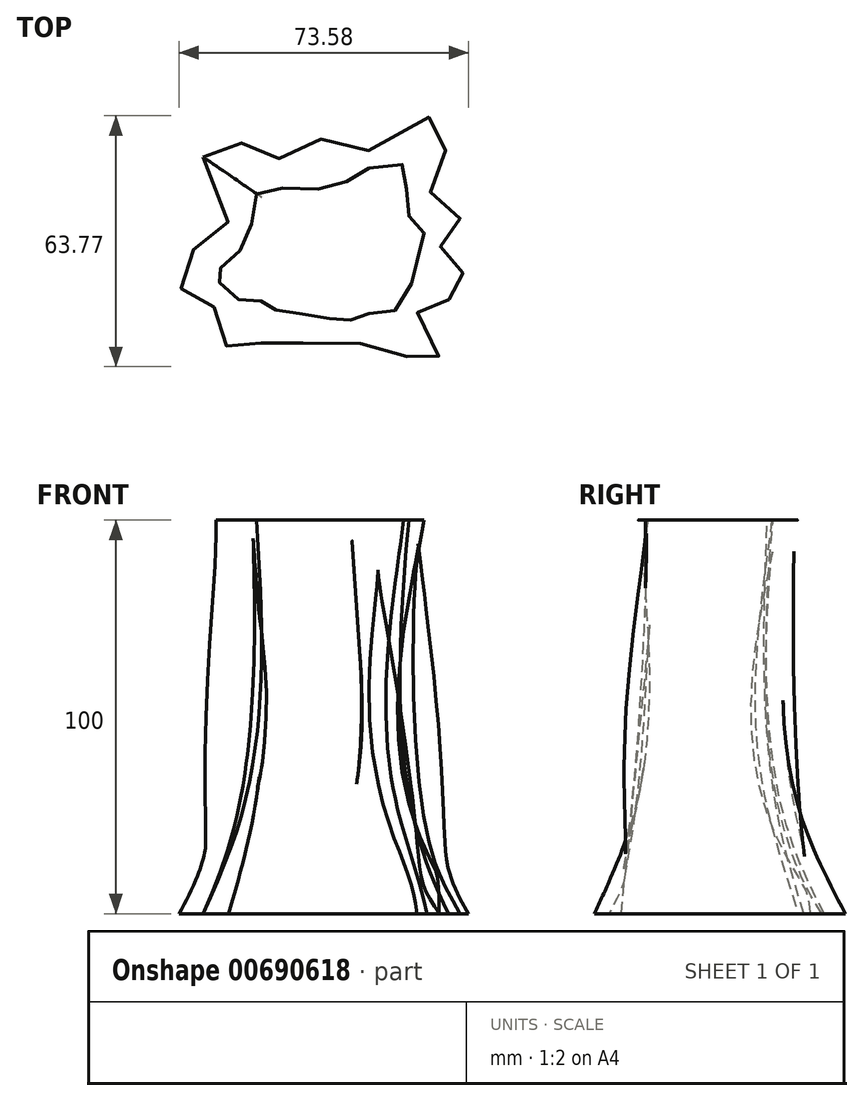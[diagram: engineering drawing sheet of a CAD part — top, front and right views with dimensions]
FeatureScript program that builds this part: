
annotation { "Feature Type Name" : "Feature", "Feature Type Description" : "" }
export const myFeature = defineFeature(function(context is Context, id is Id, definition is map)
    precondition{}
    {
        {
            var Q0;
            Q0=qCreatedBy(makeId("Top.planeOp"),FACE);
            var sketch = newSketch(context, id + "F0", { "sketchPlane" : qUnion([Q0])});
            skFitSpline(sketch, "E0", {"points": [v(-31.72, 26.3) * mm, v(-25.3, 7.86) * mm, v(-34.11, 2.83) * mm, v(-37.88, -4.72) * mm, v(-34.74, -9.75) * mm, v(-28.45, -12.26) * mm, v(-26.77, -20.11) * mm, v(-21.81, -23.2) * mm, v(-15.88, -20.43) * mm, v(-8.2, -20.73) * mm, v(6.04, -21.09) * mm, v(17.8, -22.59) * mm, v(23.98, -26.92) * mm, v(28.31, -23.2) * mm, v(22.74, -13.3) * mm, v(24.24, -10.32) * mm, v(33.88, -8.97) * mm, v(35.12, -4.02) * mm, v(28.77, 0) * mm, v(29.55, 5.26) * mm, v(33.26, 8.97) * mm, v(31.4, 15.16) * mm, v(25.22, 18.26) * mm, v(30.17, 28.78) * mm, v(27.7, 36.82) * mm, v(10.98, 28.16) * mm, v(0, 30.63) * mm, v(-8.2, 28.78) * mm, v(-16.25, 25.06) * mm, v(-24.3, 31.25) * mm, v(-31.72, 26.3) * mm]});
            skSolve(sketch);
        }
        {
            var Q0;
            Q0=qCreatedBy(makeId("Top.planeOp"),FACE);
            cPlane(context, id + "F1", {"entities" : qUnion([Q0]), "cplaneType" : CPlaneType.OFFSET, "offset" : 100 * mm, "width" : 150 * mm, "height" : 150 * mm});
        }
        {
            var Q0;
            Q0=qCreatedBy(id+"F1.planeOp",FACE);
            var sketch = newSketch(context, id + "F2", { "sketchPlane" : qUnion([Q0])});
            skFitSpline(sketch, "E1", {"points": [v(-17.91, 17.21) * mm, v(-19.82, 6.71) * mm, v(-25.23, 0) * mm, v(-28.41, -3.78) * mm, v(-26.5, -6.65) * mm, v(-20.27, -10.83) * mm, v(-15.32, -10.21) * mm, v(-12.19, -13.33) * mm, v(-3.57, -13.3) * mm, v(4.48, -15.78) * mm, v(7.86, -13.33) * mm, v(15.02, -13.8) * mm, v(21.22, -5.7) * mm, v(22.65, 0) * mm, v(24.08, 8.62) * mm, v(19.31, 12.92) * mm, v(20.26, 23.42) * mm, v(10.24, 23.42) * mm, v(3.56, 19.6) * mm, v(-8.37, 18.17) * mm, v(-17.91, 17.21) * mm]});
            skSolve(sketch);
        }
        {
            var Q0;
            Q0=qCreatedBy(makeId("Top.planeOp"),FACE);
            cPlane(context, id + "F3", {"entities" : qUnion([Q0]), "cplaneType" : CPlaneType.OFFSET, "offset" : 20 * mm, "width" : 150 * mm, "height" : 150 * mm});
        }
        {
            var Q0;
            Q0=qCreatedBy(id+"F3.planeOp",FACE);
            var sketch = newSketch(context, id + "F4", { "sketchPlane" : qUnion([Q0])});
            skFitSpline(sketch, "E2", {"points": [v(-24.3, 17.64) * mm, v(-20.04, 9.69) * mm, v(-20.89, 6.57) * mm, v(-22.45, 5.1) * mm, v(-26.85, 2.31) * mm, v(-30.11, -1.42) * mm, v(-30.68, -2.56) * mm, v(-30.96, -4.55) * mm, v(-28.41, -6.82) * mm, v(-25.57, -9.37) * mm, v(-23.59, -14.48) * mm, v(-19.33, -18) * mm, v(-12.92, -17.5) * mm, v(-6.17, -17.67) * mm, v(0, -18.34) * mm, v(6.63, -17.84) * mm, v(12.22, -18.51) * mm, v(14.71, -17.92) * mm, v(22.44, -18.65) * mm, v(16.55, -10.42) * mm, v(19.93, -9.07) * mm, v(26.34, -7.72) * mm, v(29.54, -6.03) * mm, v(28.53, -3.33) * mm, v(24.65, 1.9) * mm, v(23.3, 5.1) * mm, v(25.22, 10.83) * mm, v(21.28, 12.87) * mm, v(19.59, 16.92) * mm, v(22.8, 26.53) * mm, v(21.1, 27.2) * mm, v(15.16, 25.3) * mm, v(12.84, 25.69) * mm, v(5.25, 19.1) * mm, v(3.56, 21.35) * mm, v(-5.1, 19.5) * mm, v(-10.68, 19.1) * mm, v(-20.58, 22.59) * mm, v(-24.3, 17.64) * mm]});
            skSolve(sketch);
        }
        {
            var Q0;
            Q0=makeQuery(id+"F0.imprint","IMPRINT",FACE,{"disambiguationData":[TD([[makeQuery(id+"F0.imprint","IMPRINT",EDGE,{"derivedFrom":sQuery(id+"F0.wireOp",EDGE,"E0")}),1.0]])]});
            var Q1;
            Q1=makeQuery(id+"F4.imprint","IMPRINT",FACE,{"disambiguationData":[TD([[makeQuery(id+"F4.imprint","IMPRINT",EDGE,{"derivedFrom":sQuery(id+"F4.wireOp",EDGE,"E2")}),1.0]])]});
            var Q2;
            Q2=makeQuery(id+"F2.imprint","IMPRINT",FACE,{"disambiguationData":[TD([[makeQuery(id+"F2.imprint","IMPRINT",EDGE,{"derivedFrom":sQuery(id+"F2.wireOp",EDGE,"E1")}),1.0]])]});
            loft(context, id + "F5", {"sheetProfilesArray" : [{ "sheetProfileEntities" : qUnion([Q0]) }, { "sheetProfileEntities" : qUnion([Q1]) }, { "sheetProfileEntities" : qUnion([Q2]) }]});
        }
    });
